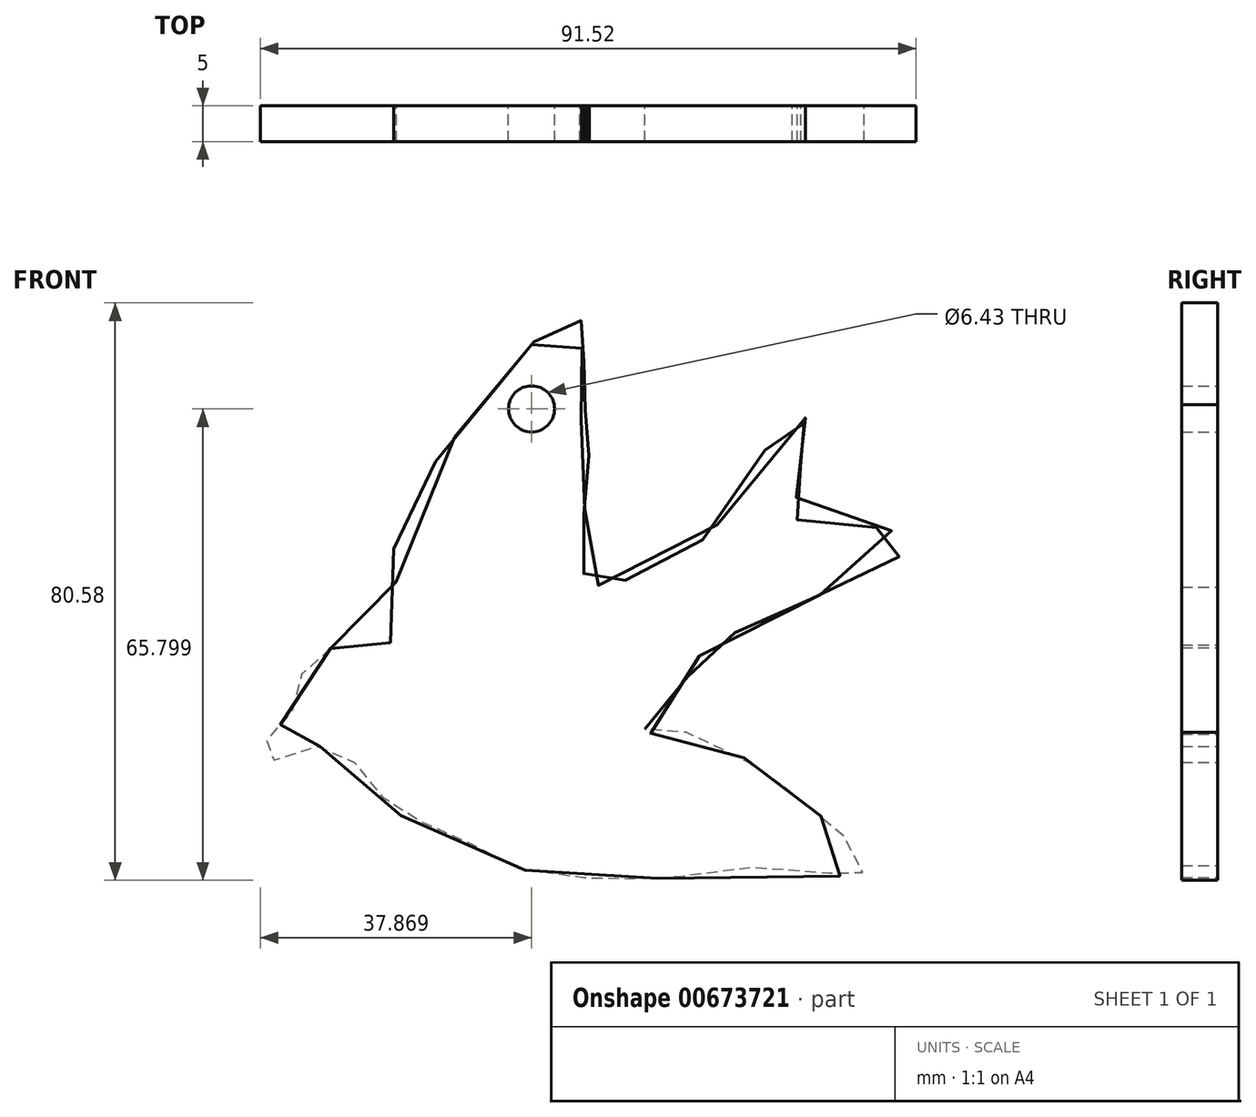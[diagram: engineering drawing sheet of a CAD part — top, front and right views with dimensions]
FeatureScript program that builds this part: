
annotation { "Feature Type Name" : "Feature", "Feature Type Description" : "" }
export const myFeature = defineFeature(function(context is Context, id is Id, definition is map)
    precondition{}
    {
        {
            var Q0;
            Q0=qCreatedBy(makeId("Front.planeOp"),FACE);
            var sketch = newSketch(context, id + "F0", { "sketchPlane" : qUnion([Q0])});
            skFitSpline(sketch, "E0", {"points": [v(-39.93, 2.34) * mm, v(-43.11, 0) * mm, v(-44.8, -3.27) * mm, v(-45.54, -6.82) * mm, v(-48.16, -9.44) * mm, v(-49.65, -13.37) * mm, v(-46.48, -12.62) * mm, v(-41.43, -11.3) * mm, v(-37.69, -12.8) * mm, v(-34.14, -15.98) * mm, v(-30.96, -20.47) * mm, v(-24.6, -22.53) * mm, v(-18.62, -26.08) * mm, v(-9.65, -29.26) * mm, v(0, -29.63) * mm, v(3.44, -29.82) * mm, v(11.66, -29.07) * mm, v(26.8, -28.32) * mm, v(34.47, -29.82) * mm, v(32.97, -26.45) * mm, v(31.3, -23.27) * mm, v(26.43, -19.54) * mm, v(23.81, -17.1) * mm, v(22.5, -16.54) * mm, v(18.58, -13.74) * mm, v(16.71, -12.06) * mm, v(13.53, -11.3) * mm, v(10.35, -9.44) * mm, v(4.56, -9.44) * mm, v(4, -8.13) * mm, v(8.67, -3.65) * mm, v(10.54, 0) * mm, v(12.6, 2.15) * mm, v(21.2, 7.01) * mm, v(26.62, 9.07) * mm, v(35.4, 13.37) * mm, v(41.76, 17.1) * mm, v(37.46, 18.97) * mm, v(32.23, 19.54) * mm, v(24.75, 20.66) * mm, v(25.3, 24.02) * mm, v(25.68, 27.39) * mm, v(25.3, 29.63) * mm, v(25.3, 31.87) * mm, v(26.24, 34.12) * mm, v(25.68, 36.36) * mm, v(17.64, 24.96) * mm, v(11.48, 17.1) * mm, v(3.25, 12.43) * mm, v(-1.8, 11.3) * mm, v(-4.79, 11.12) * mm, v(-4.23, 14.49) * mm, v(-4.79, 18.23) * mm, v(-4.41, 22.34) * mm, v(-4.23, 26.26) * mm, v(-3.85, 29.63) * mm, v(-4.41, 33) * mm, v(-4.97, 34.68) * mm, v(-4.04, 36.55) * mm, v(-5.16, 39.16) * mm, v(-4.6, 42.15) * mm, v(-4.97, 43.84) * mm, v(-4.41, 45.15) * mm, v(-4.97, 47.76) * mm, v(-5.16, 50.57) * mm, v(-12.64, 43.84) * mm, v(-14.88, 40.1) * mm, v(-18.8, 36.73) * mm, v(-23.86, 30.2) * mm, v(-30.59, 20.47) * mm, v(-30.77, 10.56) * mm, v(-31.9, 2.71) * mm, v(-33.58, 2.71) * mm, v(-39.93, 2.34) * mm]});
            skCircle(sketch, "E1", {"center": v(-11.9, 35.8) * mm, "radius": 3.22 * mm});
            skSolve(sketch);
        }
        {
            var Q0;
            Q0 = qSketchRegion(id + "F0", true);
            extrude(context, id + "F1", {"entities" : qUnion([Q0]), "depth" : 5 * mm, "offsetDistance" : 25.4 * mm});
        }
        {
            var Q0;
            Q0 = qSketchRegion(id + "F0", true);
            extrude(context, id + "F2", {"entities" : qUnion([Q0]), "operationType" : NewBodyOperationType.ADD, "depth" : 5 * mm, "offsetDistance" : 25 * mm});
        }
    });
